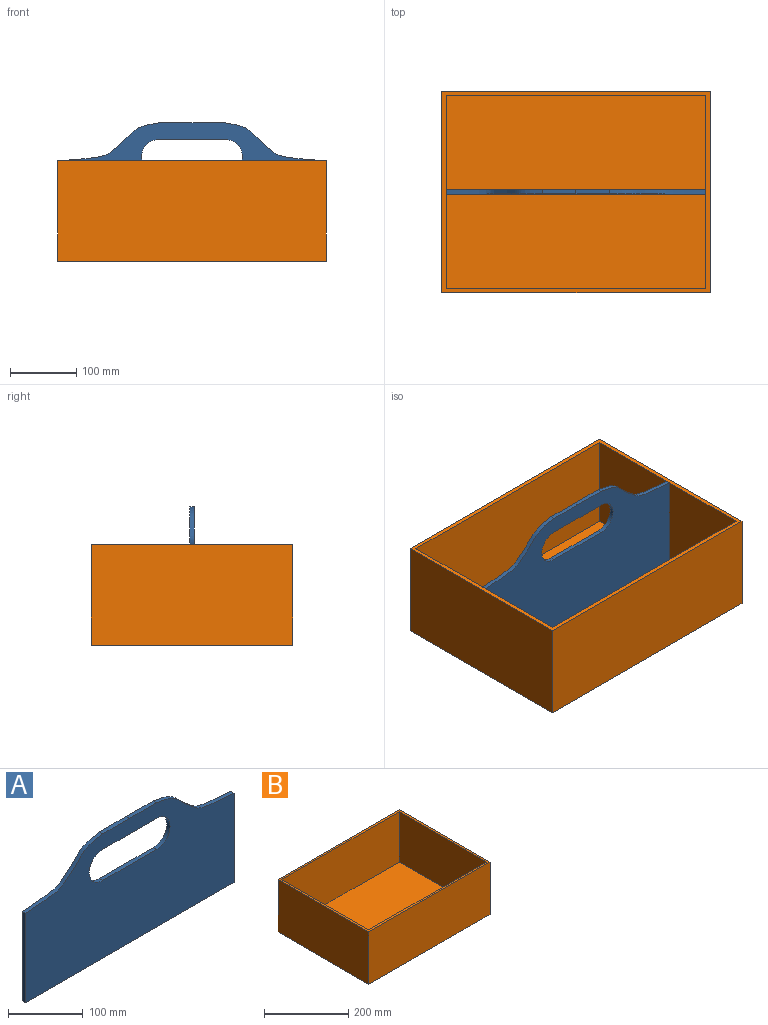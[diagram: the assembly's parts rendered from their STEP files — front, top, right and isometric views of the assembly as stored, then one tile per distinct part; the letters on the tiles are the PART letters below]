
ASSEMBLY  parts=2 mates=1
PART A: 13 faces, bbox 393.7x6.4x203.2 mm
  f0: plane 146.05x6.35mm, normal (-1,0,0), area 927.4mm2, adj f1,f10,f11,f12
  f1: plane 393.7x6.35mm, normal (0,0,-1), area 2500mm2, adj f0,f2,f11,f12
  f2: plane 146.05x6.35mm, normal (1,0,0), area 927.4mm2, adj f1,f3,f11,f12
  f3: extruded ~146.05x57.15mm, area 1033.3mm2, adj f2,f4,f11,f12
  f4: plane 50.8x6.35mm, normal (0,0,1), area 322.6mm2, adj f3,f5,f11,f12
  f5: plane 50.8x6.35mm, normal (0,0,1), area 322.6mm2, adj f4,f10,f11,f12
  f6: cylinder r=25.4mm len=50.8mm, axis (0,1,0), area 506.7mm2, adj f7,f9,f11,f12
  f7: plane 101.6x6.35mm, normal (0,0,1), area 645.2mm2, adj f6,f8,f11,f12
  f8: cylinder r=25.4mm len=50.8mm, axis (0,1,0), area 506.7mm2, adj f7,f9,f11,f12
  f9: plane 101.6x6.35mm, normal (0,0,-1), area 645.2mm2, adj f6,f8,f11,f12
  f10: extruded ~146.05x57.15mm, area 1033.3mm2, adj f0,f5,f11,f12
  f11: plane 393.7x203.2mm, normal (0,-1,0), area 62605.5mm2, adj f0,f1,f2,f3,f4,f5,f6,f7
  f12: plane 393.7x203.2mm, normal (0,1,0), area 62605.5mm2, adj f0,f1,f2,f3,f4,f5,f6,f7
PART B: 11 faces, bbox 406.4x304.8x152.4 mm
  f0: plane 406.4x304.8mm, normal (0,0,1), area 8870.9mm2, adj f1,f2,f3,f4,f6,f7,f8,f9
  f1: plane 304.8x152.4mm, normal (-1,0,0), area 46451.5mm2, adj f0,f2,f4,f5
  f2: plane 406.4x152.4mm, normal (0,-1,0), area 61935.4mm2, adj f0,f1,f3,f5
  f3: plane 304.8x152.4mm, normal (1,0,0), area 46451.5mm2, adj f0,f2,f4,f5
  f4: plane 406.4x152.4mm, normal (0,1,0), area 61935.4mm2, adj f0,f1,f3,f5
  f5: plane 406.4x304.8mm, normal (0,0,-1), area 123870.7mm2, adj f1,f2,f3,f4
  f6: plane 393.7x146.05mm, normal (0,1,0), area 57499.9mm2, adj f0,f7,f9,f10
  f7: plane 292.1x146.05mm, normal (-1,0,0), area 42661.2mm2, adj f0,f6,f8,f10
  f8: plane 393.7x146.05mm, normal (0,-1,0), area 57499.9mm2, adj f0,f7,f9,f10
  f9: plane 292.1x146.05mm, normal (1,0,0), area 42661.2mm2, adj f0,f6,f8,f10
  f10: plane 393.7x292.1mm, normal (0,0,1), area 114999.8mm2, adj f6,f7,f8,f9
PLACE A t=(20.35,54.22,90.69)mm
PLACE B t=(20.35,51.05,-17.26)mm
MATE fastened A.f1 <-> B.f10  axis (0,0,-1) through (20.35,51.05,-10.91)mm
